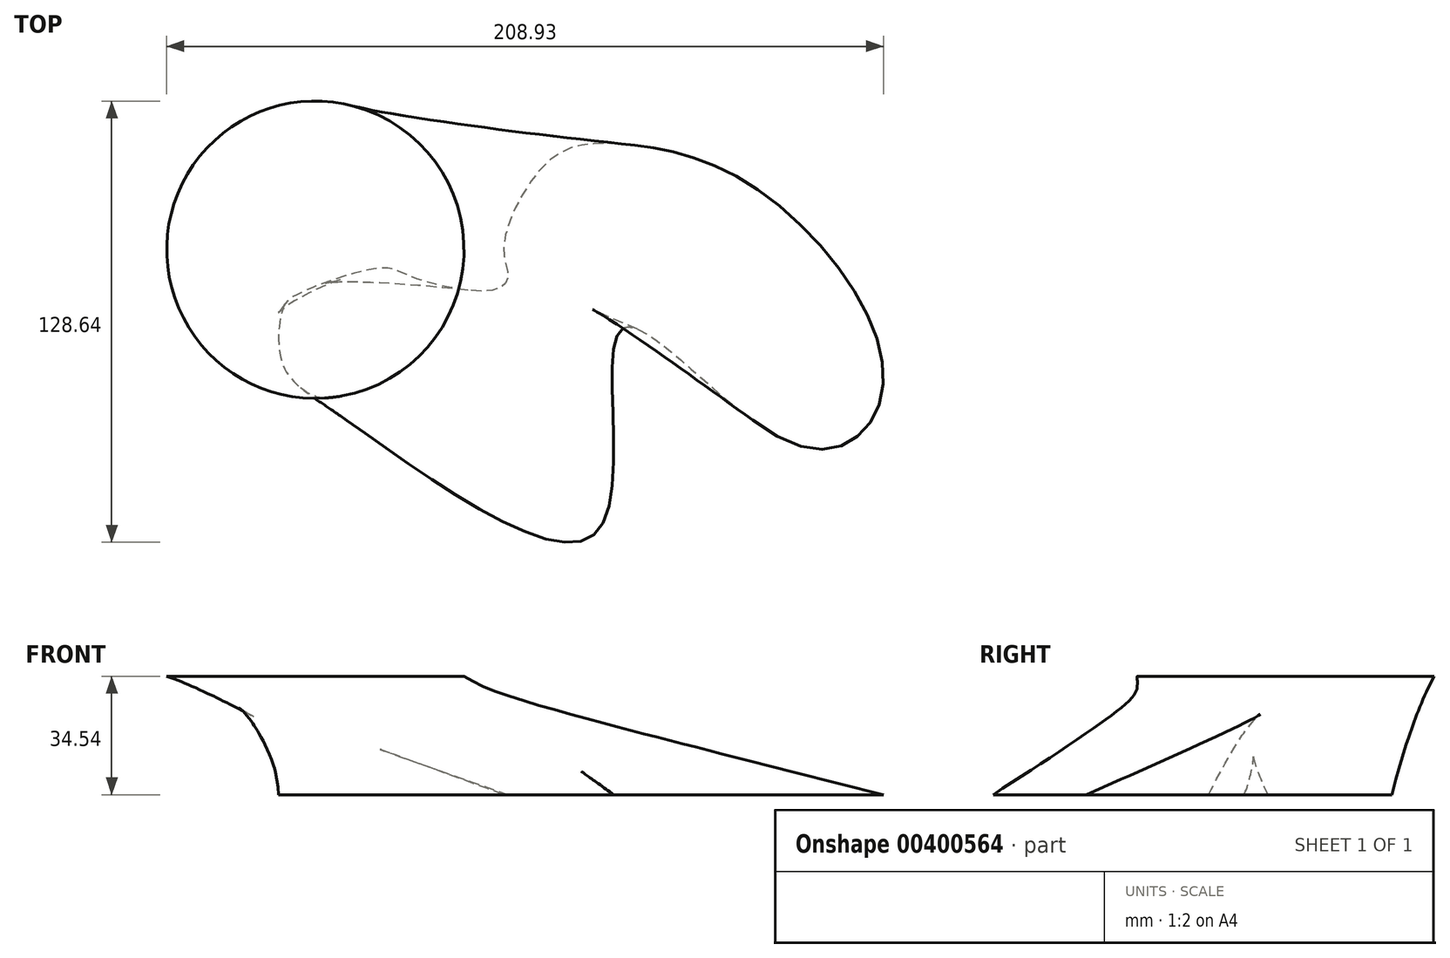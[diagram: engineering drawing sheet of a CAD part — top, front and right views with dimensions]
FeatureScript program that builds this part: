
annotation { "Feature Type Name" : "Feature", "Feature Type Description" : "" }
export const myFeature = defineFeature(function(context is Context, id is Id, definition is map)
    precondition{}
    {
        {
            var Q0;
            Q0=qCreatedBy(makeId("Top.planeOp"),FACE);
            cPlane(context, id + "F0", {"entities" : qUnion([Q0]), "cplaneType" : CPlaneType.OFFSET, "offset" : 34.54 * mm, "width" : 152.4 * mm, "height" : 152.4 * mm});
        }
        {
            var Q0;
            Q0=qCreatedBy(id+"F0.planeOp",FACE);
            var sketch = newSketch(context, id + "F1", { "sketchPlane" : qUnion([Q0])});
            skCircle(sketch, "E0", {"center": v(-108.53, 67.95) * mm, "radius": 43.33 * mm});
            skSolve(sketch);
        }
        {
            var Q0;
            Q0=qCreatedBy(makeId("Top.planeOp"),FACE);
            var sketch = newSketch(context, id + "F2", { "sketchPlane" : qUnion([Q0])});
            skFitSpline(sketch, "E1", {"points": [v(-99.36, 18.2) * mm, v(-26.6, -14.46) * mm, v(-19.2, 44.8) * mm, v(32.82, 10.65) * mm, v(57, 28.98) * mm, v(20.06, 85.74) * mm, v(-22.05, 98.86) * mm, v(-40.58, 93.71) * mm, v(-53.56, 69.02) * mm, v(-52.4, 60.13) * mm, v(-56.27, 56.27) * mm, v(-80.22, 59.93) * mm, v(-89.22, 62.65) * mm, v(-113.52, 55.07) * mm, v(-118.11, 50.48) * mm, v(-118.31, 35.22) * mm, v(-99.36, 18.2) * mm]});
            skSolve(sketch);
        }
        {
            var Q0;
            Q0=makeQuery(id+"F2.imprint","IMPRINT",FACE,{"disambiguationData":[TD([[makeQuery(id+"F2.imprint","IMPRINT",EDGE,{"derivedFrom":sQuery(id+"F2.wireOp",EDGE,"E1")}),1.0]])]});
            var Q1;
            Q1=makeQuery(id+"F1.imprint","IMPRINT",FACE,{"disambiguationData":[TD([[makeQuery(id+"F1.imprint","IMPRINT",EDGE,{"derivedFrom":sQuery(id+"F1.wireOp",EDGE,"E0")}),1.0]])]});
            loft(context, id + "F3", {"sheetProfilesArray" : [{ "sheetProfileEntities" : qUnion([Q0]) }, { "sheetProfileEntities" : qUnion([Q1]) }]});
        }
    });
